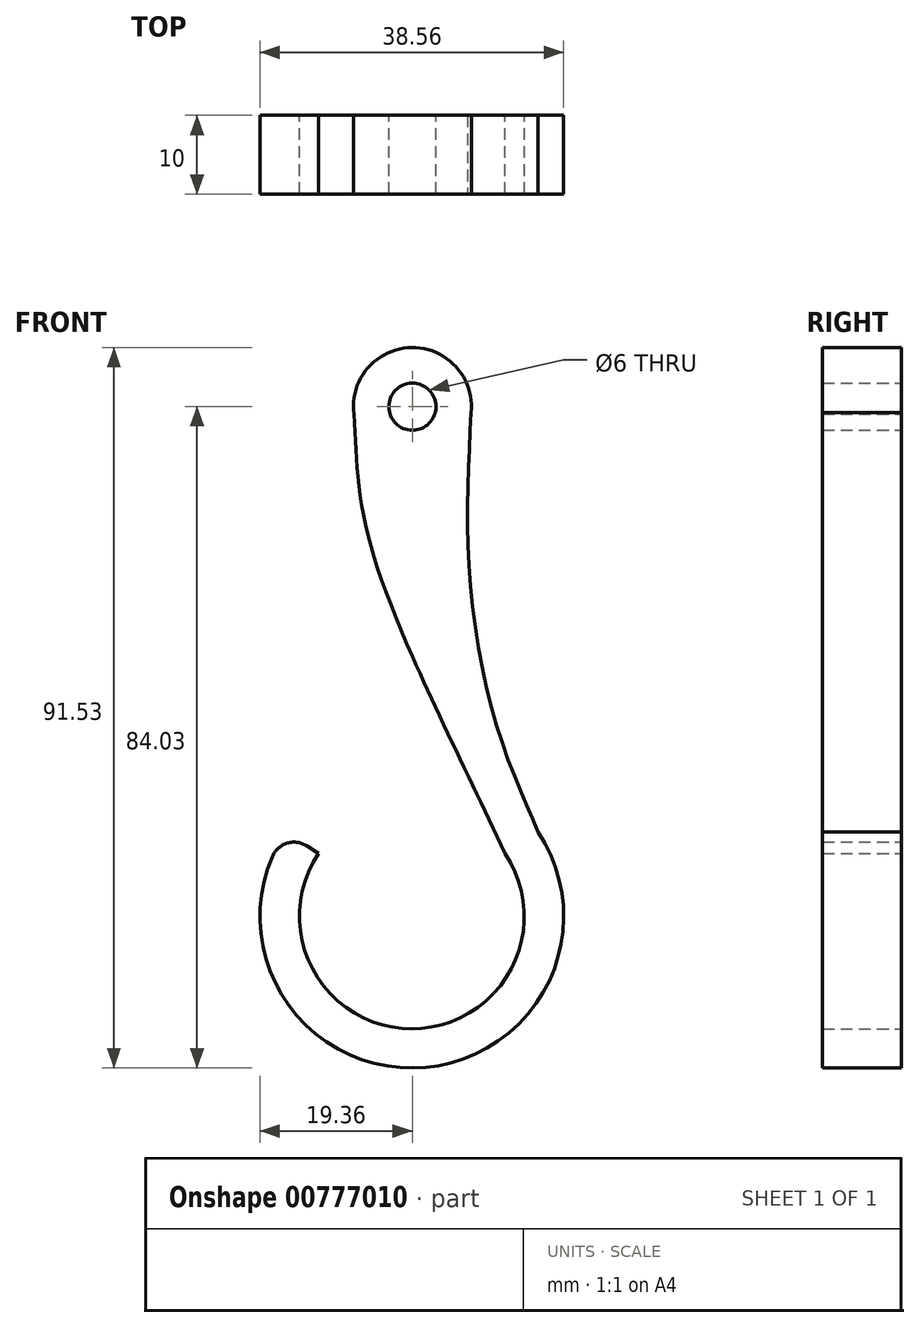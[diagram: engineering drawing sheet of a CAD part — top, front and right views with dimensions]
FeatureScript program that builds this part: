
annotation { "Feature Type Name" : "Feature", "Feature Type Description" : "" }
export const myFeature = defineFeature(function(context is Context, id is Id, definition is map)
    precondition{}
    {
        {
            var Q0;
            Q0=qCreatedBy(makeId("Front.planeOp"),FACE);
            var sketch = newSketch(context, id + "F0", { "sketchPlane" : qUnion([Q0])});
            skCircle(sketch, "E0", {"center": v(0, 0) * mm, "radius": 3 * mm});
            skCircle(sketch, "E1", {"center": v(0, 0) * mm, "radius": 7.5 * mm});
            skLineSegment(sketch, "E2", {"start": v(0, 0) * mm, "end": v(0, -82.55) * mm});
            skArc(sketch, "E3", {"start": v(-11.94, -56.8) * mm, "mid": v(-0.08, -79.03) * mm, "end": v(11.78, -56.8) * mm});
            skArc(sketch, "E4.0", {"start": v(-16.09, -54) * mm, "mid": v(-0.08, -84.03) * mm, "end": v(15.93, -54) * mm});
            skLineSegment(sketch, "E5", {"start": v(-16.09, -54) * mm, "end": v(-11.94, -56.8) * mm});
            skFitSpline(sketch, "E6", {"points": [v(-7.5, 0) * mm, v(-5.25, -17.85) * mm, v(11.78, -56.8) * mm], "startDerivative": vector(2.99, -43.7) * mm, "endDerivative": vector(31.01, -66.49) * mm});
            skFitSpline(sketch, "E7", {"points": [v(7.5, 0) * mm, v(7.11, -19.3) * mm, v(10.84, -40.97) * mm, v(15.93, -54) * mm], "startDerivative": vector(-2.65, -53.15) * mm, "endDerivative": vector(15.6, -38.56) * mm});
            skSolve(sketch);
        }
        {
            var Q0;
            {var subQ0=sQuery(id+"F0.wireOp",EDGE,"E6");var subQ1=sQuery(id+"F0.wireOp",EDGE,"E1");var subQ2=makeQuery(id+"F0.imprint","INTERSECT",VERTEX,{"disambiguationData":[OD(0.0)],"derivedFrom":[subQ1,subQ0]});Q0=makeQuery(id+"F0.imprint","IMPRINT",FACE,{"disambiguationData":[TD([[makeQuery(id+"F0.imprint","IMPRINT",EDGE,{"disambiguationData":[TD([[subQ2,-1.0]])],"derivedFrom":subQ1}),1.0]])]});}
            var Q1;
            {var subQ0=sQuery(id+"F0.wireOp",EDGE,"E7");var subQ1=sQuery(id+"F0.wireOp",EDGE,"E1");var subQ2=makeQuery(id+"F0.imprint","INTERSECT",VERTEX,{"disambiguationData":[OD(0.0)],"derivedFrom":[subQ1,subQ0]});Q1=makeQuery(id+"F0.imprint","IMPRINT",FACE,{"disambiguationData":[TD([[makeQuery(id+"F0.imprint","IMPRINT",EDGE,{"disambiguationData":[TD([[subQ2,1.0]])],"derivedFrom":subQ1}),1.0]])]});}
            var Q2;
            {var subQ0=sQuery(id+"F0.wireOp",EDGE,"E6");var subQ1=sQuery(id+"F0.wireOp",EDGE,"E1");var subQ2=makeQuery(id+"F0.imprint","INTERSECT",VERTEX,{"disambiguationData":[OD(1.0)],"derivedFrom":[subQ1,subQ0]});Q2=makeQuery(id+"F0.imprint","IMPRINT",FACE,{"disambiguationData":[TD([[makeQuery(id+"F0.imprint","IMPRINT",EDGE,{"disambiguationData":[TD([[subQ2,-1.0]])],"derivedFrom":subQ1}),-1.0]])]});}
            var Q3;
            {var subQ11=sQuery(id+"F0.wireOp",EDGE,"E4.0");Q3=makeQuery(id+"F0.imprint","IMPRINT",FACE,{"disambiguationData":[TD([[makeQuery(id+"F0.imprint","IMPRINT",EDGE,{"derivedFrom":subQ11}),1.0]])]});}
            var Q4;
            Q4=makeQuery(id+"F0.imprint","IMPRINT",FACE,{"disambiguationData":[TD([[makeQuery(id+"F0.imprint","IMPRINT",EDGE,{"derivedFrom":sQuery(id+"F0.wireOp",EDGE,"E0")}),-1.0]])]});
            extrude(context, id + "F1", {"entities" : qUnion([Q0, Q1, Q2, Q3, Q4]), "depth" : 10 * mm, "offsetDistance" : 25 * mm});
        }
        {
            var Q0;
            Q0=makeQuery(id+"F1.opExtrude","SWEPT_EDGE",EDGE,{"disambiguationData":[OSD([sQuery(id+"F0.wireOp",EDGE,"E4.0"),sQuery(id+"F0.wireOp",EDGE,"E5")])]});
            fillet(context, id + "F2", {"entities" : qUnion([Q0]), "radius" : 3 * mm, "tangentPropagation" : true, "allowEdgeOverflow" : false});
        }
    });
